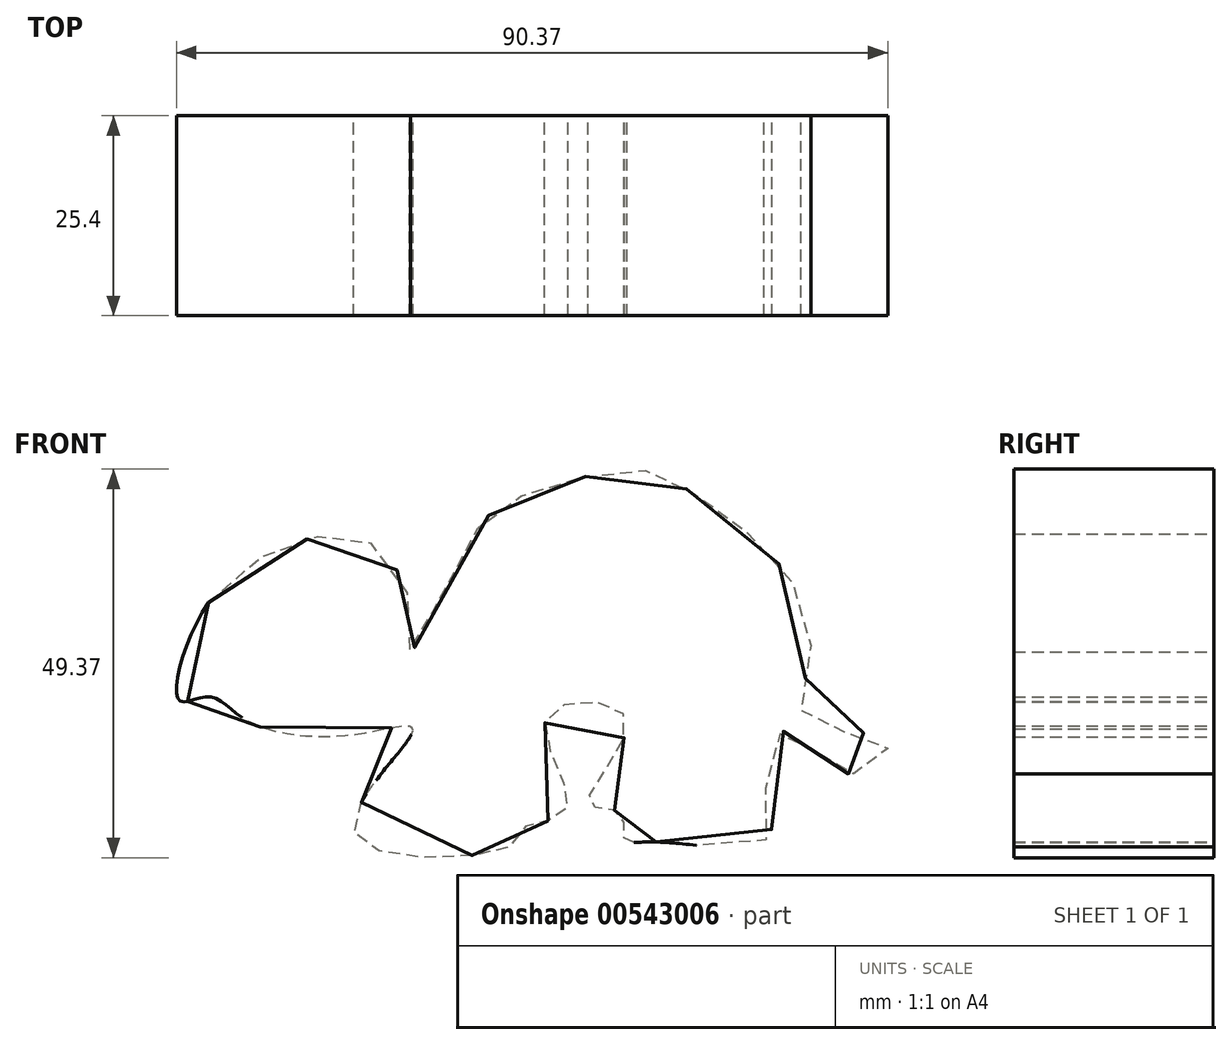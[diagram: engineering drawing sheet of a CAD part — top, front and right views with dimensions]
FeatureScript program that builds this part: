
annotation { "Feature Type Name" : "Feature", "Feature Type Description" : "" }
export const myFeature = defineFeature(function(context is Context, id is Id, definition is map)
    precondition{}
    {
        {
            var Q0;
            Q0=qCreatedBy(makeId("Front.planeOp"),FACE);
            var sketch = newSketch(context, id + "F0", { "sketchPlane" : qUnion([Q0])});
            skFitSpline(sketch, "E0", {"points": [v(-37.21, 0) * mm, v(-26.74, 7.4) * mm, v(-18.09, 8.3) * mm, v(-11.71, 0) * mm, v(-11.49, -6.27) * mm, v(-2.83, 9.67) * mm, v(4, 14) * mm, v(16.52, 16.96) * mm, v(24.26, 14) * mm, v(34.28, 6.03) * mm, v(39.28, -5.36) * mm, v(38.83, -15.37) * mm, v(48.4, -17.2) * mm, v(48.16, -20.38) * mm, v(41.1, -20.84) * mm, v(37, -16.06) * mm, v(33.36, -20.84) * mm, v(33.82, -29.94) * mm, v(19.25, -30.4) * mm, v(15.6, -29.94) * mm, v(15.15, -26.76) * mm, v(11.05, -25.4) * mm, v(15.83, -14.7) * mm, v(5.82, -14.46) * mm, v(8.32, -26.07) * mm, v(2.4, -28.8) * mm, v(1.72, -30.63) * mm, v(-18.54, -29.49) * mm, v(-11.26, -16.28) * mm, v(-18.32, -16.74) * mm, v(-32.43, -14.92) * mm, v(-37.21, -11.96) * mm, v(-40.89, -12.41) * mm, v(-37.21, 0) * mm]});
            skSolve(sketch);
        }
        {
            var Q0;
            Q0 = qSketchRegion(id + "F0", true);
            extrude(context, id + "F1", {"entities" : qUnion([Q0]), "depth" : 25.4 * mm, "offsetDistance" : 25.4 * mm});
        }
    });
